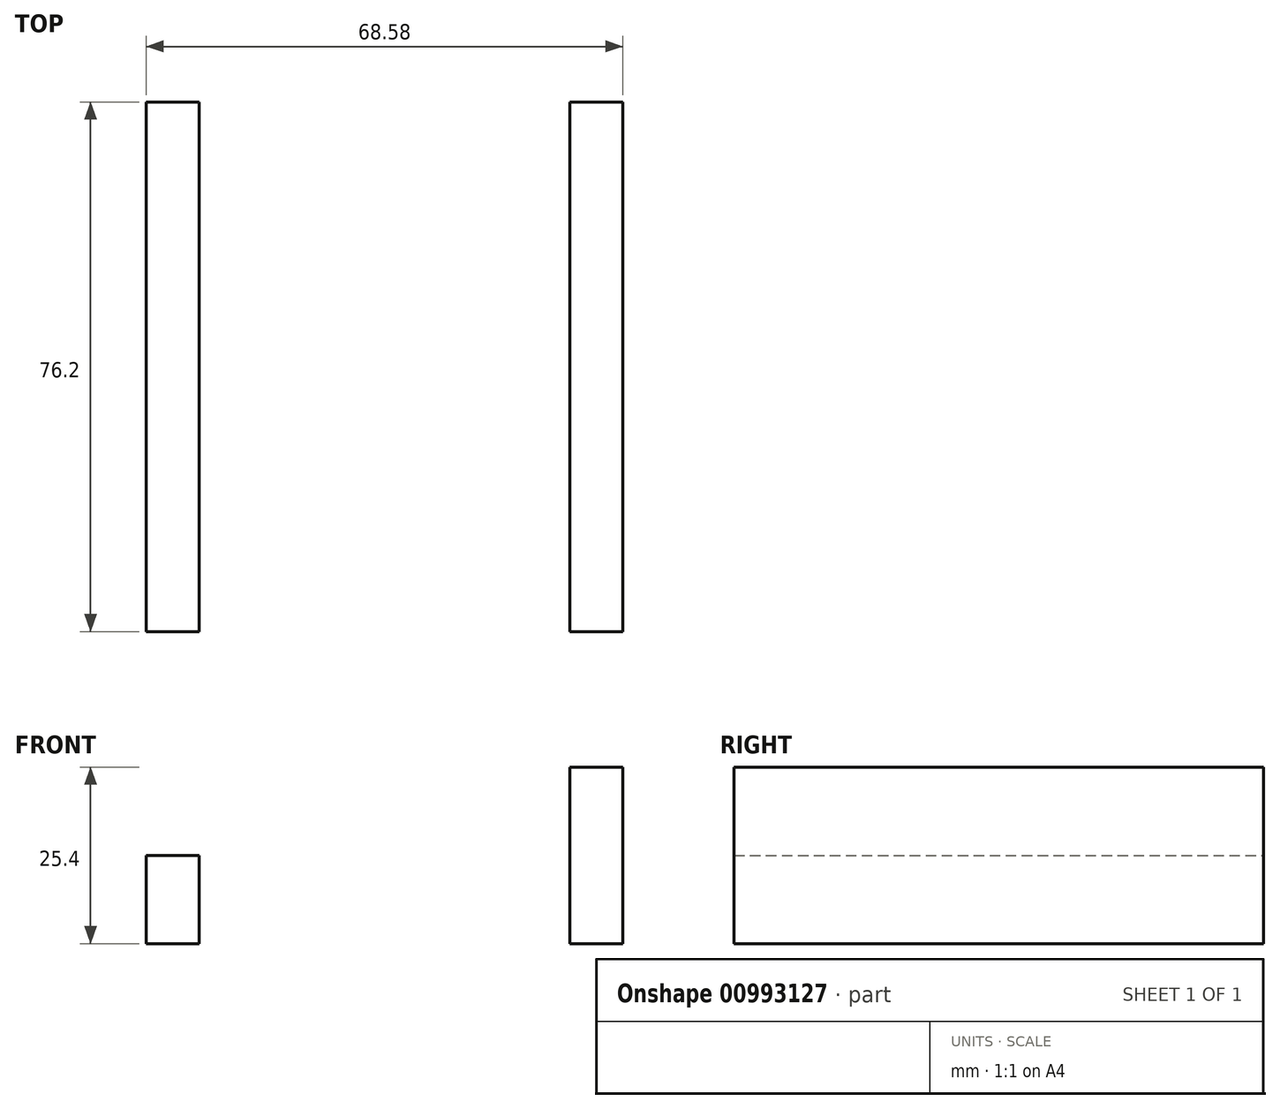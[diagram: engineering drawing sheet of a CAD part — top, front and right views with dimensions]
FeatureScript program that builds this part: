
annotation { "Feature Type Name" : "Feature", "Feature Type Description" : "" }
export const myFeature = defineFeature(function(context is Context, id is Id, definition is map)
    precondition{}
    {
        {
            var Q0;
            Q0=qCreatedBy(makeId("Front.planeOp"),FACE);
            var sketch = newSketch(context, id + "F0", { "sketchPlane" : qUnion([Q0])});
            skLineSegment(sketch, "E0.bottom", {"start": v(-40.8, 46.14) * mm, "end": v(27.79, 46.14) * mm});
            skLineSegment(sketch, "E0.top", {"start": v(-40.8, 33.44) * mm, "end": v(27.79, 33.44) * mm});
            skLineSegment(sketch, "E0.left", {"start": v(-40.8, 46.14) * mm, "end": v(-40.8, 33.44) * mm});
            skLineSegment(sketch, "E0.right", {"start": v(27.79, 46.14) * mm, "end": v(27.79, 33.44) * mm});
            skLineSegment(sketch, "E1.bottom", {"start": v(-33.17, 46.14) * mm, "end": v(20.17, 46.14) * mm});
            skLineSegment(sketch, "E1.top", {"start": v(-33.17, 33.44) * mm, "end": v(20.17, 33.44) * mm});
            skLineSegment(sketch, "E1.left", {"start": v(-33.17, 46.14) * mm, "end": v(-33.17, 33.44) * mm});
            skLineSegment(sketch, "E1.right", {"start": v(20.17, 46.14) * mm, "end": v(20.17, 33.44) * mm});
            skLineSegment(sketch, "E2.bottom", {"start": v(-40.8, 46.14) * mm, "end": v(-33.17, 46.14) * mm});
            skLineSegment(sketch, "E2.top", {"start": v(-40.8, 58.84) * mm, "end": v(-33.17, 58.84) * mm});
            skLineSegment(sketch, "E2.left", {"start": v(-40.8, 46.14) * mm, "end": v(-40.8, 58.84) * mm});
            skLineSegment(sketch, "E2.right", {"start": v(-33.17, 46.14) * mm, "end": v(-33.17, 58.84) * mm});
            skLineSegment(sketch, "E3.bottom", {"start": v(27.79, 58.84) * mm, "end": v(20.17, 58.84) * mm});
            skLineSegment(sketch, "E3.top", {"start": v(27.79, 46.14) * mm, "end": v(20.17, 46.14) * mm});
            skLineSegment(sketch, "E3.left", {"start": v(27.79, 58.84) * mm, "end": v(27.79, 46.14) * mm});
            skLineSegment(sketch, "E3.right", {"start": v(20.17, 58.84) * mm, "end": v(20.17, 46.14) * mm});
            skSolve(sketch);
        }
        {
            var Q0;
            Q0=makeQuery(id+"F0.imprint","IMPRINT",FACE,{"disambiguationData":[TD([[makeQuery(id+"F0.imprint","IMPRINT",EDGE,{"derivedFrom":sQuery(id+"F0.wireOp",EDGE,"E2.bottom")}),1.0]])]});
            var Q1;
            {var subQ0=sQuery(id+"F0.wireOp",EDGE,"E0.left");Q1=makeQuery(id+"F0.imprint","IMPRINT",FACE,{"disambiguationData":[TD([[makeQuery(id+"F0.imprint","IMPRINT",EDGE,{"derivedFrom":subQ0}),1.0]])]});}
            var Q2;
            Q2=makeQuery(id+"F0.imprint","IMPRINT",FACE,{"disambiguationData":[TD([[makeQuery(id+"F0.imprint","IMPRINT",EDGE,{"derivedFrom":sQuery(id+"F0.wireOp",EDGE,"E1.bottom")}),-1.0]])]});
            var Q3;
            {var subQ0=sQuery(id+"F0.wireOp",EDGE,"E0.right");Q3=makeQuery(id+"F0.imprint","IMPRINT",FACE,{"disambiguationData":[TD([[makeQuery(id+"F0.imprint","IMPRINT",EDGE,{"derivedFrom":subQ0}),-1.0]])]});}
            var Q4;
            Q4=makeQuery(id+"F0.imprint","IMPRINT",FACE,{"disambiguationData":[TD([[makeQuery(id+"F0.imprint","IMPRINT",EDGE,{"derivedFrom":sQuery(id+"F0.wireOp",EDGE,"E3.bottom")}),1.0]])]});
            extrude(context, id + "F1", {"entities" : qUnion([Q0, Q1, Q2, Q3, Q4]), "depth" : 25.4 * mm, "offsetDistance" : 25.4 * mm});
        }
        {
            var Q0;
            Q0=makeQuery(id+"F0.imprint","IMPRINT",FACE,{"disambiguationData":[TD([[makeQuery(id+"F0.imprint","IMPRINT",EDGE,{"derivedFrom":sQuery(id+"F0.wireOp",EDGE,"E2.bottom")}),1.0]])]});
            var Q1;
            {var subQ0=sQuery(id+"F0.wireOp",EDGE,"E0.left");Q1=makeQuery(id+"F0.imprint","IMPRINT",FACE,{"disambiguationData":[TD([[makeQuery(id+"F0.imprint","IMPRINT",EDGE,{"derivedFrom":subQ0}),1.0]])]});}
            var Q2;
            {var subQ0=sQuery(id+"F0.wireOp",EDGE,"E0.right");Q2=makeQuery(id+"F0.imprint","IMPRINT",FACE,{"disambiguationData":[TD([[makeQuery(id+"F0.imprint","IMPRINT",EDGE,{"derivedFrom":subQ0}),-1.0]])]});}
            var Q3;
            Q3=makeQuery(id+"F0.imprint","IMPRINT",FACE,{"disambiguationData":[TD([[makeQuery(id+"F0.imprint","IMPRINT",EDGE,{"derivedFrom":sQuery(id+"F0.wireOp",EDGE,"E3.bottom")}),1.0]])]});
            extrude(context, id + "F2", {"entities" : qUnion([Q0, Q1, Q2, Q3]), "operationType" : NewBodyOperationType.ADD, "oppositeDirection" : true, "depth" : 50.8 * mm, "offsetDistance" : 25.4 * mm});
        }
    });
